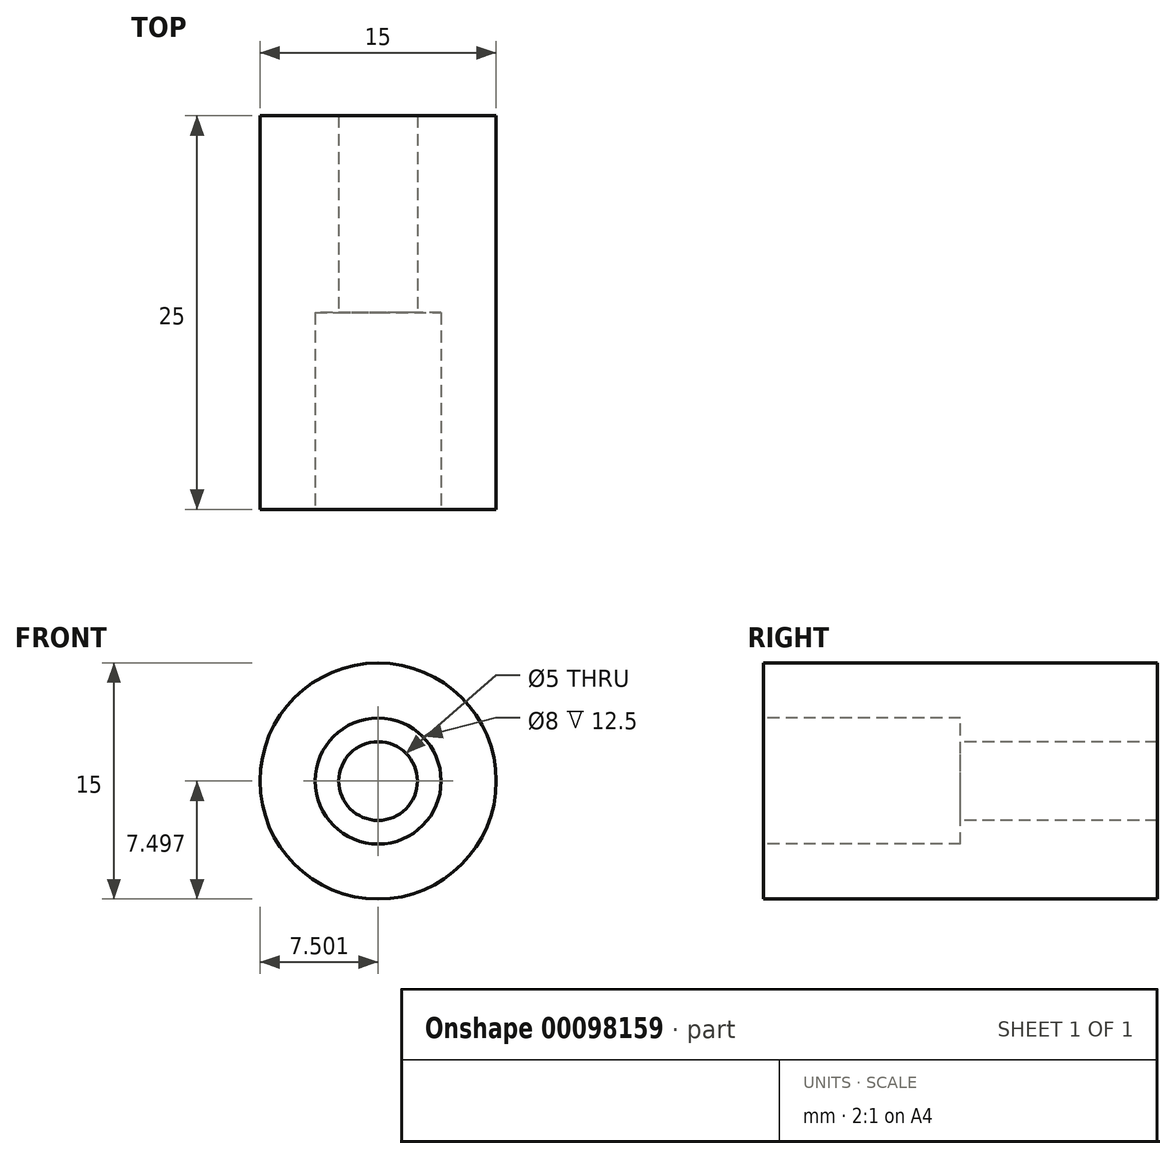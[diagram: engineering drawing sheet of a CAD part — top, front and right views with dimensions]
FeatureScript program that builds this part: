
annotation { "Feature Type Name" : "Feature", "Feature Type Description" : "" }
export const myFeature = defineFeature(function(context is Context, id is Id, definition is map)
    precondition{}
    {
        {
            var Q0;
            Q0=qCreatedBy(makeId("Front.planeOp"),FACE);
            var sketch = newSketch(context, id + "F0", { "sketchPlane" : qUnion([Q0])});
            skCircle(sketch, "E0", {"center": v(-41.75, 41.1) * mm, "radius": 7.5 * mm});
            skSolve(sketch);
        }
        {
            var Q0;
            Q0=makeQuery(id+"F0.imprint","IMPRINT",FACE,{"disambiguationData":[TD([[makeQuery(id+"F0.imprint","IMPRINT",EDGE,{"derivedFrom":sQuery(id+"F0.wireOp",EDGE,"E0")}),1.0]])]});
            extrude(context, id + "F1", {"entities" : qUnion([Q0]), "oppositeDirection" : true, "depth" : 25 * mm});
        }
        {
            var Q0;
            Q0=sQuery(id+"F0.wireOp",VERTEX,"E0.center");
            var Q1;
            Q1=makeQuery(id+"F1.opExtrude","SWEPT_BODY",BODY,{"disambiguationData":[OSD([sQuery(id+"F0.wireOp",EDGE,"E0")])]});
            hole(context, id + "F2", {"style" : HoleStyle.C_BORE, "endStyle" : HoleEndStyle.BLIND, "holeDiameter" : 5 * mm, "cBoreDiameter" : 8 * mm, "cBoreDepth" : 12.5 * mm, "holeDepth" : 25 * mm, "locations" : qUnion([Q0]), "scope" : qUnion([Q1])});
        }
    });
